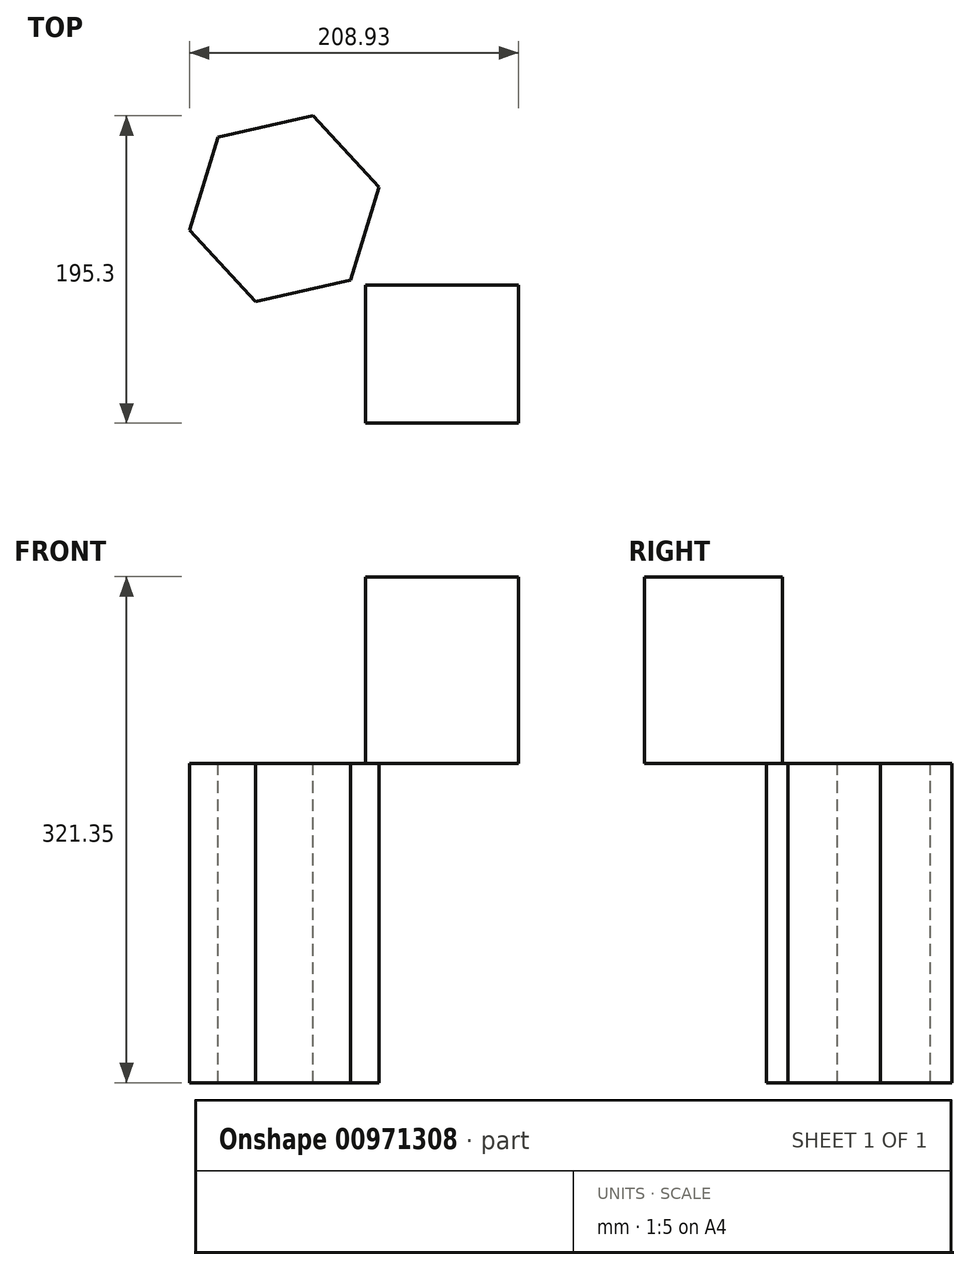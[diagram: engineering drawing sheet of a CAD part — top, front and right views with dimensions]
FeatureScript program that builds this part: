
annotation { "Feature Type Name" : "Feature", "Feature Type Description" : "" }
export const myFeature = defineFeature(function(context is Context, id is Id, definition is map)
    precondition{}
    {
        {
            var Q0;
            Q0=qCreatedBy(makeId("Top.planeOp"),FACE);
            var sketch = newSketch(context, id + "F0", { "sketchPlane" : qUnion([Q0])});
            skLineSegment(sketch, "E0.bottom", {"start": v(-26, 21.15) * mm, "end": v(71.18, 21.15) * mm});
            skLineSegment(sketch, "E0.top", {"start": v(-26, -66.53) * mm, "end": v(71.18, -66.53) * mm});
            skLineSegment(sketch, "E0.left", {"start": v(-26, 21.15) * mm, "end": v(-26, -66.53) * mm});
            skLineSegment(sketch, "E0.right", {"start": v(71.18, 21.15) * mm, "end": v(71.18, -66.53) * mm});
            skSolve(sketch);
        }
        {
            var Q0;
            Q0 = qSketchRegion(id + "F0", true);
            extrude(context, id + "F1", {"entities" : qUnion([Q0]), "depth" : 118.64 * mm, "offsetDistance" : 25.4 * mm});
        }
        {
            var Q0;
            Q0=qCreatedBy(makeId("Top.planeOp"),FACE);
            var sketch = newSketch(context, id + "F2", { "sketchPlane" : qUnion([Q0])});
            skCircle(sketch, "E1.cCircle", {"center": v(-77.54, 69.8) * mm, "radius": 53.47 * mm, "construction": true});
            skLineSegment(sketch, "E1.0", {"start": v(-59.27, 128.77) * mm, "end": v(-17.33, 83.46) * mm});
            skLineSegment(sketch, "E1.1", {"start": v(-17.33, 83.46) * mm, "end": v(-35.6, 24.48) * mm});
            skLineSegment(sketch, "E1.2", {"start": v(-35.6, 24.48) * mm, "end": v(-95.81, 10.82) * mm});
            skLineSegment(sketch, "E1.3", {"start": v(-95.81, 10.82) * mm, "end": v(-137.75, 56.13) * mm});
            skLineSegment(sketch, "E1.4", {"start": v(-137.75, 56.13) * mm, "end": v(-119.48, 115.1) * mm});
            skLineSegment(sketch, "E1.5", {"start": v(-119.48, 115.1) * mm, "end": v(-59.27, 128.77) * mm});
            skPoint(sketch, "E1.0.midPoint", {"position": v(-38.3, 106.11) * mm});
            skSolve(sketch);
        }
        {
            var Q0;
            Q0=makeQuery(id+"F2.imprint","IMPRINT",FACE,{"disambiguationData":[TD([[makeQuery(id+"F2.imprint","IMPRINT",EDGE,{"derivedFrom":sQuery(id+"F2.wireOp",EDGE,"E1.0")}),-1.0]])]});
            extrude(context, id + "F3", {"entities" : qUnion([Q0]), "oppositeDirection" : true, "depth" : 202.71 * mm, "offsetDistance" : 25.4 * mm});
        }
    });
